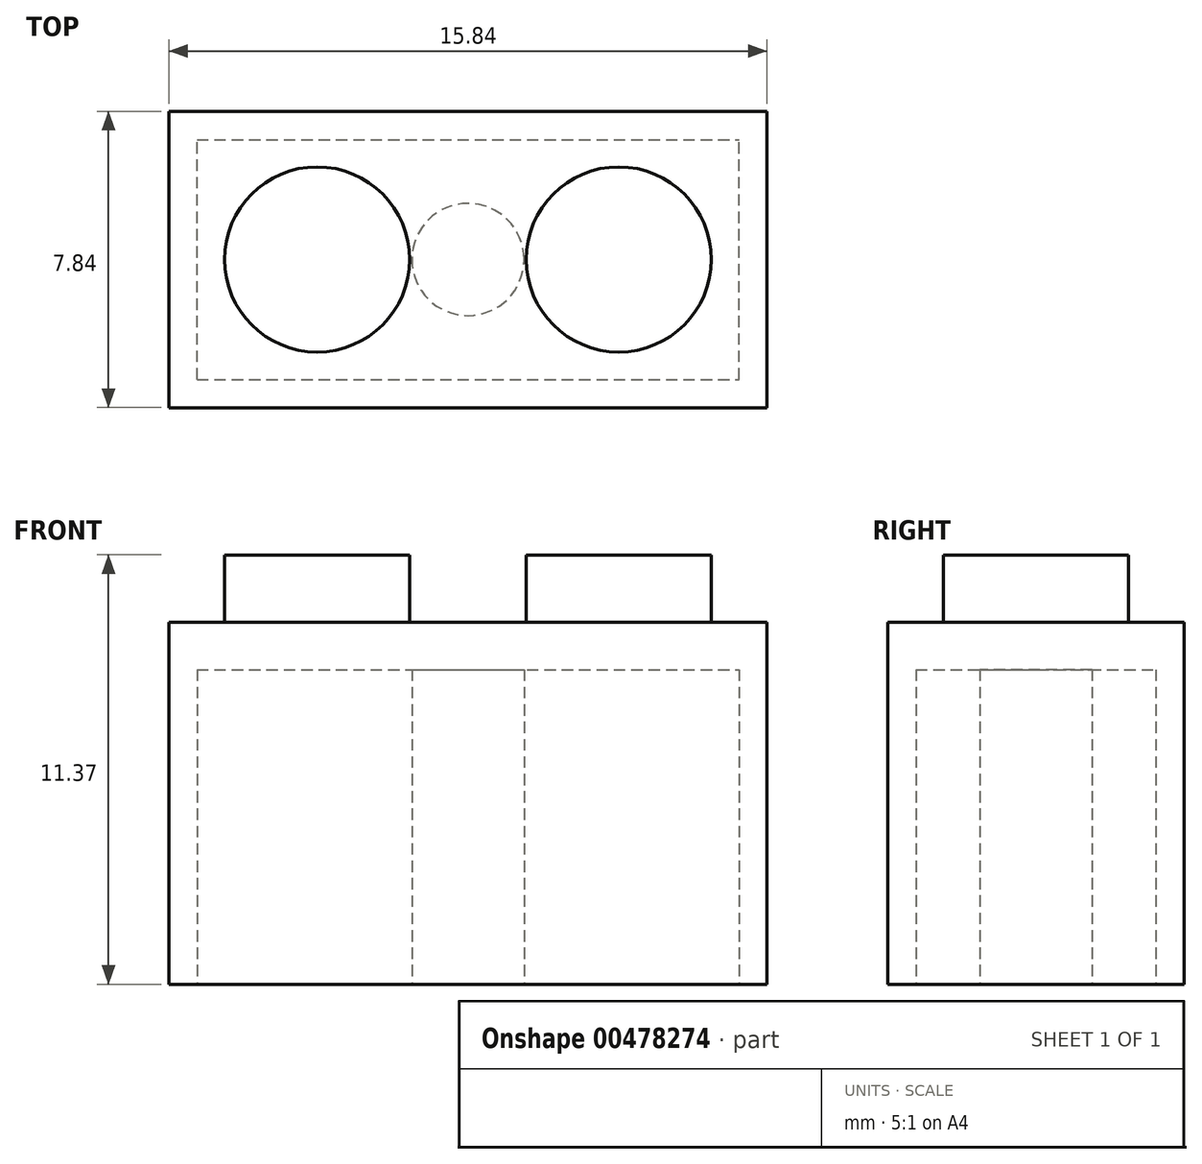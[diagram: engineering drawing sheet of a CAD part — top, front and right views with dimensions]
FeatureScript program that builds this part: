
annotation { "Feature Type Name" : "Feature", "Feature Type Description" : "" }
export const myFeature = defineFeature(function(context is Context, id is Id, definition is map)
    precondition{}
    {
        {
            var Q0;
            Q0=qCreatedBy(makeId("Top.planeOp"),FACE);
            var sketch = newSketch(context, id + "F0", { "sketchPlane" : qUnion([Q0])});
            skLineSegment(sketch, "E0.bottom", {"start": v(-7.92, 3.92) * mm, "end": v(7.92, 3.92) * mm});
            skLineSegment(sketch, "E0.top", {"start": v(-7.92, -3.92) * mm, "end": v(7.92, -3.92) * mm});
            skLineSegment(sketch, "E0.left", {"start": v(-7.92, 3.92) * mm, "end": v(-7.92, -3.92) * mm});
            skLineSegment(sketch, "E0.right", {"start": v(7.92, 3.92) * mm, "end": v(7.92, -3.92) * mm});
            skPoint(sketch, "E0.middle", {"position": v(0, 0) * mm});
            skSolve(sketch);
        }
        {
            var Q0;
            Q0=makeQuery(id+"F0.imprint","IMPRINT",FACE,{"disambiguationData":[TD([[makeQuery(id+"F0.imprint","IMPRINT",EDGE,{"derivedFrom":sQuery(id+"F0.wireOp",EDGE,"E0.bottom")}),-1.0]])]});
            extrude(context, id + "F1", {"entities" : qUnion([Q0]), "depth" : 9.6 * mm});
        }
        {
            var Q0;
            Q0=makeQuery(id+"F1.opExtrude","CAP_FACE",FACE,{"disambiguationData":[OSD([sQuery(id+"F0.wireOp",EDGE,"E0.bottom"),sQuery(id+"F0.wireOp",EDGE,"E0.top"),sQuery(id+"F0.wireOp",EDGE,"E0.left"),sQuery(id+"F0.wireOp",EDGE,"E0.right")])],"isStart":false});
            var sketch = newSketch(context, id + "F2", { "sketchPlane" : qUnion([Q0])});
            skCircle(sketch, "E1", {"center": v(-4, 0) * mm, "radius": 2.45 * mm});
            skSolve(sketch);
        }
        {
            var Q0;
            Q0=makeQuery(id+"F2.imprint","IMPRINT",FACE,{"disambiguationData":[TD([[makeQuery(id+"F2.imprint","IMPRINT",EDGE,{"derivedFrom":sQuery(id+"F2.wireOp",EDGE,"E1")}),-1.0]])]});
            var sketch = newSketch(context, id + "F3", { "sketchPlane" : qUnion([Q0])});
            skCircle(sketch, "E2", {"center": v(4, 0) * mm, "radius": 2.45 * mm});
            skSolve(sketch);
        }
        {
            var Q0;
            Q0=makeQuery(id+"F2.imprint","IMPRINT",FACE,{"disambiguationData":[TD([[makeQuery(id+"F2.imprint","IMPRINT",EDGE,{"derivedFrom":sQuery(id+"F2.wireOp",EDGE,"E1")}),1.0]])]});
            extrude(context, id + "F4", {"entities" : qUnion([Q0]), "operationType" : NewBodyOperationType.ADD, "depth" : 1.78 * mm});
        }
        {
            var Q0;
            Q0=makeQuery(id+"F3.imprint","IMPRINT",FACE,{"disambiguationData":[TD([[makeQuery(id+"F3.imprint","IMPRINT",EDGE,{"derivedFrom":sQuery(id+"F3.wireOp",EDGE,"E2")}),1.0]])]});
            extrude(context, id + "F5", {"entities" : qUnion([Q0]), "operationType" : NewBodyOperationType.ADD, "depth" : 1.78 * mm});
        }
        {
            var Q0;
            Q0=makeQuery(id+"F1.opExtrude","CAP_FACE",FACE,{"disambiguationData":[OSD([sQuery(id+"F0.wireOp",EDGE,"E0.bottom"),sQuery(id+"F0.wireOp",EDGE,"E0.top"),sQuery(id+"F0.wireOp",EDGE,"E0.left"),sQuery(id+"F0.wireOp",EDGE,"E0.right")])],"isStart":true});
            var sketch = newSketch(context, id + "F6", { "sketchPlane" : qUnion([Q0])});
            skLineSegment(sketch, "E3.bottom", {"start": v(-7.18, 3.17) * mm, "end": v(7.18, 3.17) * mm});
            skLineSegment(sketch, "E3.top", {"start": v(-7.18, -3.17) * mm, "end": v(7.18, -3.17) * mm});
            skLineSegment(sketch, "E3.left", {"start": v(-7.18, 3.17) * mm, "end": v(-7.18, -3.17) * mm});
            skLineSegment(sketch, "E3.right", {"start": v(7.18, 3.17) * mm, "end": v(7.18, -3.17) * mm});
            skPoint(sketch, "E3.middle", {"position": v(0, 0) * mm});
            skSolve(sketch);
        }
        {
            var Q0;
            Q0=makeQuery(id+"F6.imprint","IMPRINT",FACE,{"disambiguationData":[TD([[makeQuery(id+"F6.imprint","IMPRINT",EDGE,{"derivedFrom":sQuery(id+"F6.wireOp",EDGE,"E3.bottom")}),-1.0]])]});
            var sketch = newSketch(context, id + "F7", { "sketchPlane" : qUnion([Q0])});
            skCircle(sketch, "E4", {"center": v(0, 0) * mm, "radius": 1.49 * mm});
            skSolve(sketch);
        }
        {
            var Q0;
            Q0=makeQuery(id+"F6.imprint","IMPRINT",FACE,{"disambiguationData":[TD([[makeQuery(id+"F6.imprint","IMPRINT",EDGE,{"derivedFrom":sQuery(id+"F6.wireOp",EDGE,"E3.bottom")}),-1.0]])]});
            extrude(context, id + "F8", {"entities" : qUnion([Q0]), "operationType" : NewBodyOperationType.REMOVE, "oppositeDirection" : true, "depth" : 8.33 * mm, "offsetDistance" : 25.4 * mm});
        }
        {
            var Q0;
            Q0=makeQuery(id+"F7.imprint","IMPRINT",FACE,{"disambiguationData":[TD([[makeQuery(id+"F7.imprint","IMPRINT",EDGE,{"derivedFrom":sQuery(id+"F7.wireOp",EDGE,"E4")}),1.0]])]});
            extrude(context, id + "F9", {"entities" : qUnion([Q0]), "operationType" : NewBodyOperationType.ADD, "oppositeDirection" : true, "depth" : 8.33 * mm, "offsetDistance" : 25.4 * mm});
        }
    });
